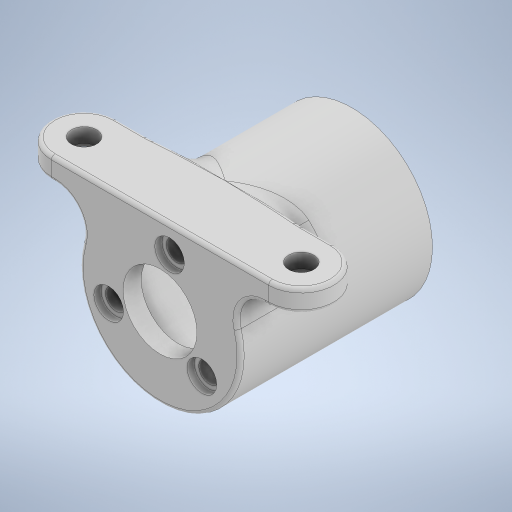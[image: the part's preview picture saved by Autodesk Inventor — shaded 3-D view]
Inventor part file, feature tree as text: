
AUTODESK INVENTOR PART (.ipt)
format: ipt  version: 2024.2 (Build 282272000, 272)  size: 420,352 bytes
history: native  units: mm
features: sketch x7, extrude x5, hole x2, fillet x2, plane x1, chamfer x1
ambient origin geometry x8: Origin, YZ Plane, XZ Plane, XY Plane, X Axis, Y Axis, Z Axis, Center Point
bodies: Solid1 (feature_tree)
feature tree (18):
  extrude  "Extrusion1"  Depth=2.9mm
  extrude  "Extrusion2"  Depth=30.0mm TaperAngle=360.0deg
  extrude  "Extrusion3"  Depth=22.25mm
  plane  "Work Plane1"
  extrude  "Extrusion4"  Depth=4.1mm
  extrude  "Extrusion5"  Depth=20.25mm
  hole  "Hole1"  [1 undecoded]
  hole  "Hole2"  [1 undecoded]
  fillet  "Fillet1"  Radius=15.0mm
  fillet  "Fillet2"  Radius=3.0mm
  chamfer  "Chamfer1"  Distance=1.5mm
  sketch  "Sketch1"  dims[d0=10.2mm d1=2.9mm]
  sketch  "Sketch2"  dims[d2=7.55mm d3=30.0mm d5=360.0deg]
  sketch  "Sketch3"  dims[d7=1.745329mm d8=22.25mm]
  sketch  "Sketch4"  dims[d9=1.5mm d10=0.0mm d11=4.1mm]
  sketch  "Sketch5"  dims[d12=1.0mm d13=0.0mm d14=20.25mm]
  sketch  "Sketch6"  dims[d15=24.0mm d16=0.0mm d17=11.125mm]
  sketch  "Sketch7"  dims[d18=9.0mm d19=30.0mm d20=15.0mm d21=3.0mm d22=0.0mm d23=1.5mm d24=0.0mm d25=2.9mm d26=6.0mm d27=4.1mm d28=1.0mm d29=90.0deg d30=8.0mm d31=20.594885mm d32=3.5mm d33=6.0mm d34=5.25mm d35=1.0mm d36=90.0deg d37=8.0mm d38=20.594885mm d39=4.0mm d40=0.5mm d41=0.5mm d42=2.0mm d43=45.0deg]
note: 2 required parameter values undecoded (feature->parameter linkage not recoverable at this tier; creation-order binding heuristic only, values carry confidence <= 0.55)
